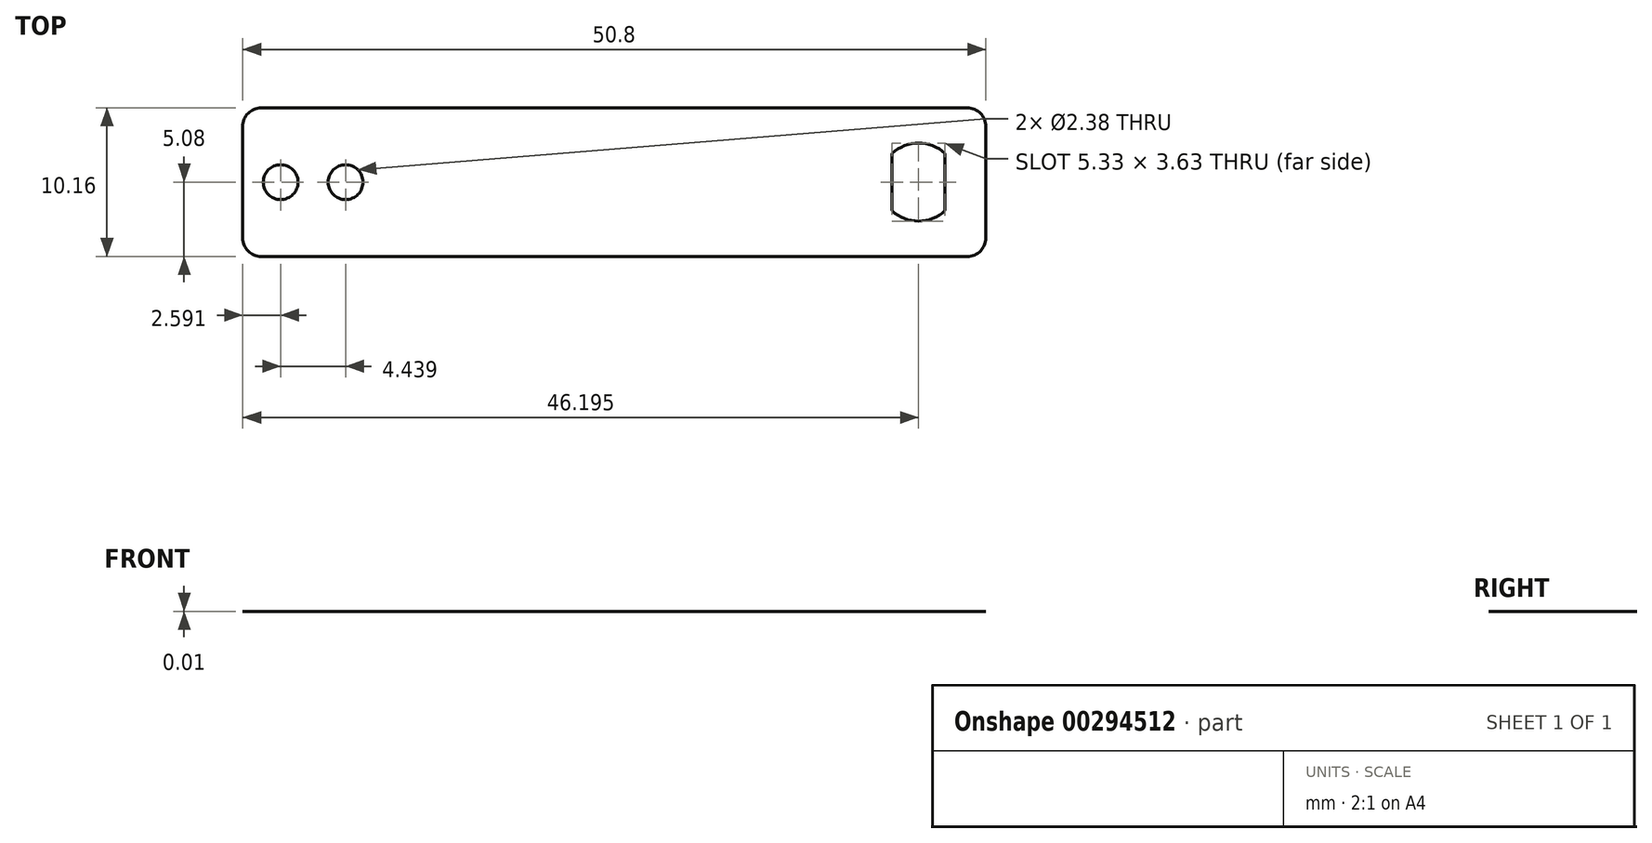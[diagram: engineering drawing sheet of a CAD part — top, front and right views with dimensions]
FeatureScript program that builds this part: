
annotation { "Feature Type Name" : "Feature", "Feature Type Description" : "" }
export const myFeature = defineFeature(function(context is Context, id is Id, definition is map)
    precondition{}
    {
        {
            var Q0;
            Q0=qCreatedBy(makeId("Top.planeOp"),FACE);
            var sketch = newSketch(context, id + "F0", { "sketchPlane" : qUnion([Q0])});
            skLineSegment(sketch, "E0.bottom", {"start": v(25.4, 5.08) * mm, "end": v(-25.4, 5.08) * mm});
            skLineSegment(sketch, "E0.top", {"start": v(25.4, -5.08) * mm, "end": v(-25.4, -5.08) * mm});
            skLineSegment(sketch, "E0.left", {"start": v(25.4, 5.08) * mm, "end": v(25.4, -5.08) * mm});
            skLineSegment(sketch, "E0.right", {"start": v(-25.4, 5.08) * mm, "end": v(-25.4, -5.08) * mm});
            skPoint(sketch, "E0.middle", {"position": v(0, 0) * mm});
            skLineSegment(sketch, "E1", {"start": v(-25.4, 0) * mm, "end": v(25.4, 0) * mm});
            skCircle(sketch, "E2", {"center": v(-22.8, 0) * mm, "radius": 1.2 * mm});
            skCircle(sketch, "E3", {"center": v(-18.37, 0) * mm, "radius": 1.2 * mm});
            skCircle(sketch, "E4", {"center": v(20.8, 0) * mm, "radius": 2.67 * mm});
            skLineSegment(sketch, "E5", {"start": v(18.98, 1.95) * mm, "end": v(18.98, -1.95) * mm});
            skLineSegment(sketch, "E6", {"start": v(22.61, 1.95) * mm, "end": v(22.61, -1.95) * mm});
            skSolve(sketch);
        }
        {
            var Q0;
            {var subQ12=sQuery(id+"F0.wireOp",EDGE,"E0.bottom");Q0=makeQuery(id+"F0.imprint","IMPRINT",FACE,{"disambiguationData":[TD([[makeQuery(id+"F0.imprint","IMPRINT",EDGE,{"derivedFrom":subQ12}),1.0]])]});}
            var Q1;
            {var subQ0=sQuery(id+"F0.wireOp",EDGE,"E4");var subQ1=sQuery(id+"F0.wireOp",EDGE,"E1");var subQ2=makeQuery(id+"F0.imprint","INTERSECT",VERTEX,{"disambiguationData":[OD(0.0)],"derivedFrom":[subQ1,subQ0]});Q1=makeQuery(id+"F0.imprint","IMPRINT",FACE,{"disambiguationData":[TD([[makeQuery(id+"F0.imprint","IMPRINT",EDGE,{"disambiguationData":[TD([[subQ2,-1.0]])],"derivedFrom":subQ1}),1.0]])]});}
            var Q2;
            {var subQ0=sQuery(id+"F0.wireOp",EDGE,"E4");var subQ1=sQuery(id+"F0.wireOp",EDGE,"E1");var subQ2=makeQuery(id+"F0.imprint","INTERSECT",VERTEX,{"disambiguationData":[OD(0.0)],"derivedFrom":[subQ1,subQ0]});Q2=makeQuery(id+"F0.imprint","IMPRINT",FACE,{"disambiguationData":[TD([[makeQuery(id+"F0.imprint","IMPRINT",EDGE,{"disambiguationData":[TD([[subQ2,-1.0]])],"derivedFrom":subQ1}),-1.0]])]});}
            var Q3;
            {var subQ0=sQuery(id+"F0.wireOp",EDGE,"E6");var subQ1=sQuery(id+"F0.wireOp",EDGE,"E1");var subQ2=makeQuery(id+"F0.imprint","INTERSECT",VERTEX,{"derivedFrom":[subQ1,subQ0]});Q3=makeQuery(id+"F0.imprint","IMPRINT",FACE,{"disambiguationData":[TD([[makeQuery(id+"F0.imprint","IMPRINT",EDGE,{"disambiguationData":[TD([[subQ2,-1.0]])],"derivedFrom":subQ1}),1.0]])]});}
            var Q4;
            {var subQ0=sQuery(id+"F0.wireOp",EDGE,"E6");var subQ1=sQuery(id+"F0.wireOp",EDGE,"E1");var subQ2=makeQuery(id+"F0.imprint","INTERSECT",VERTEX,{"derivedFrom":[subQ1,subQ0]});Q4=makeQuery(id+"F0.imprint","IMPRINT",FACE,{"disambiguationData":[TD([[makeQuery(id+"F0.imprint","IMPRINT",EDGE,{"disambiguationData":[TD([[subQ2,-1.0]])],"derivedFrom":subQ1}),-1.0]])]});}
            var Q5;
            {var subQ9=sQuery(id+"F0.wireOp",EDGE,"E0.top");Q5=makeQuery(id+"F0.imprint","IMPRINT",FACE,{"disambiguationData":[TD([[makeQuery(id+"F0.imprint","IMPRINT",EDGE,{"derivedFrom":subQ9}),-1.0]])]});}
            extrude(context, id + "F1", {"entities" : qUnion([Q0, Q1, Q2, Q3, Q4, Q5]), "depth" : 3 / 406.4 * mm});
        }
        {
            var Q0;
            Q0=makeQuery(id+"F1.opExtrude","SWEPT_EDGE",EDGE,{"disambiguationData":[OSD([sQuery(id+"F0.wireOp",EDGE,"E0.bottom"),sQuery(id+"F0.wireOp",EDGE,"E0.left")])]});
            var Q1;
            Q1=makeQuery(id+"F1.opExtrude","SWEPT_EDGE",EDGE,{"disambiguationData":[OSD([sQuery(id+"F0.wireOp",EDGE,"E0.top"),sQuery(id+"F0.wireOp",EDGE,"E0.left")])]});
            var Q2;
            Q2=makeQuery(id+"F1.opExtrude","SWEPT_EDGE",EDGE,{"disambiguationData":[OSD([sQuery(id+"F0.wireOp",EDGE,"E0.bottom"),sQuery(id+"F0.wireOp",EDGE,"E0.right")])]});
            var Q3;
            Q3=makeQuery(id+"F1.opExtrude","SWEPT_EDGE",EDGE,{"disambiguationData":[OSD([sQuery(id+"F0.wireOp",EDGE,"E0.top"),sQuery(id+"F0.wireOp",EDGE,"E0.right")])]});
            fillet(context, id + "F2", {"entities" : qUnion([Q0, Q1, Q2, Q3]), "radius" : 1.27 * mm, "tangentPropagation" : true, "allowEdgeOverflow" : false});
        }
    });
